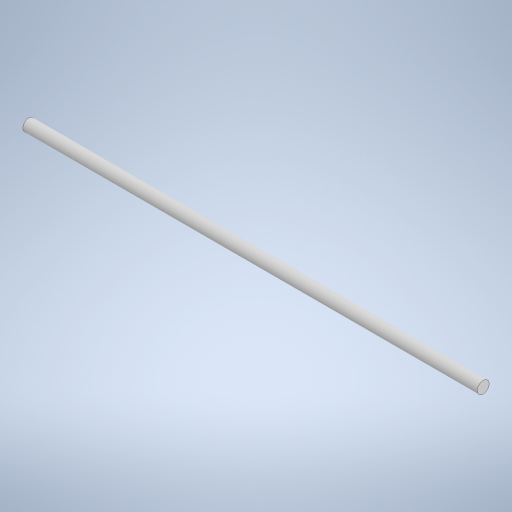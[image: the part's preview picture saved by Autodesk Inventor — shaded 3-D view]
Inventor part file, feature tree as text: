
AUTODESK INVENTOR PART (.ipt)
format: ipt  version: 2024.3 (Build 283343000, 343)  size: 233,984 bytes
history: native  units: mm
features: extrude x1, sketch x1
ambient origin geometry x8: Origin, YZ Plane, XZ Plane, XY Plane, X Axis, Y Axis, Z Axis, Center Point
bodies: Solid1 (feature_tree)
feature tree (2):
  extrude  "Extrusion1"  Depth=300.0mm TaperAngle=0.0deg
  sketch  "Sketch1"  dims[d0=8.0mm d1=300.0mm d2=0.0mm]
